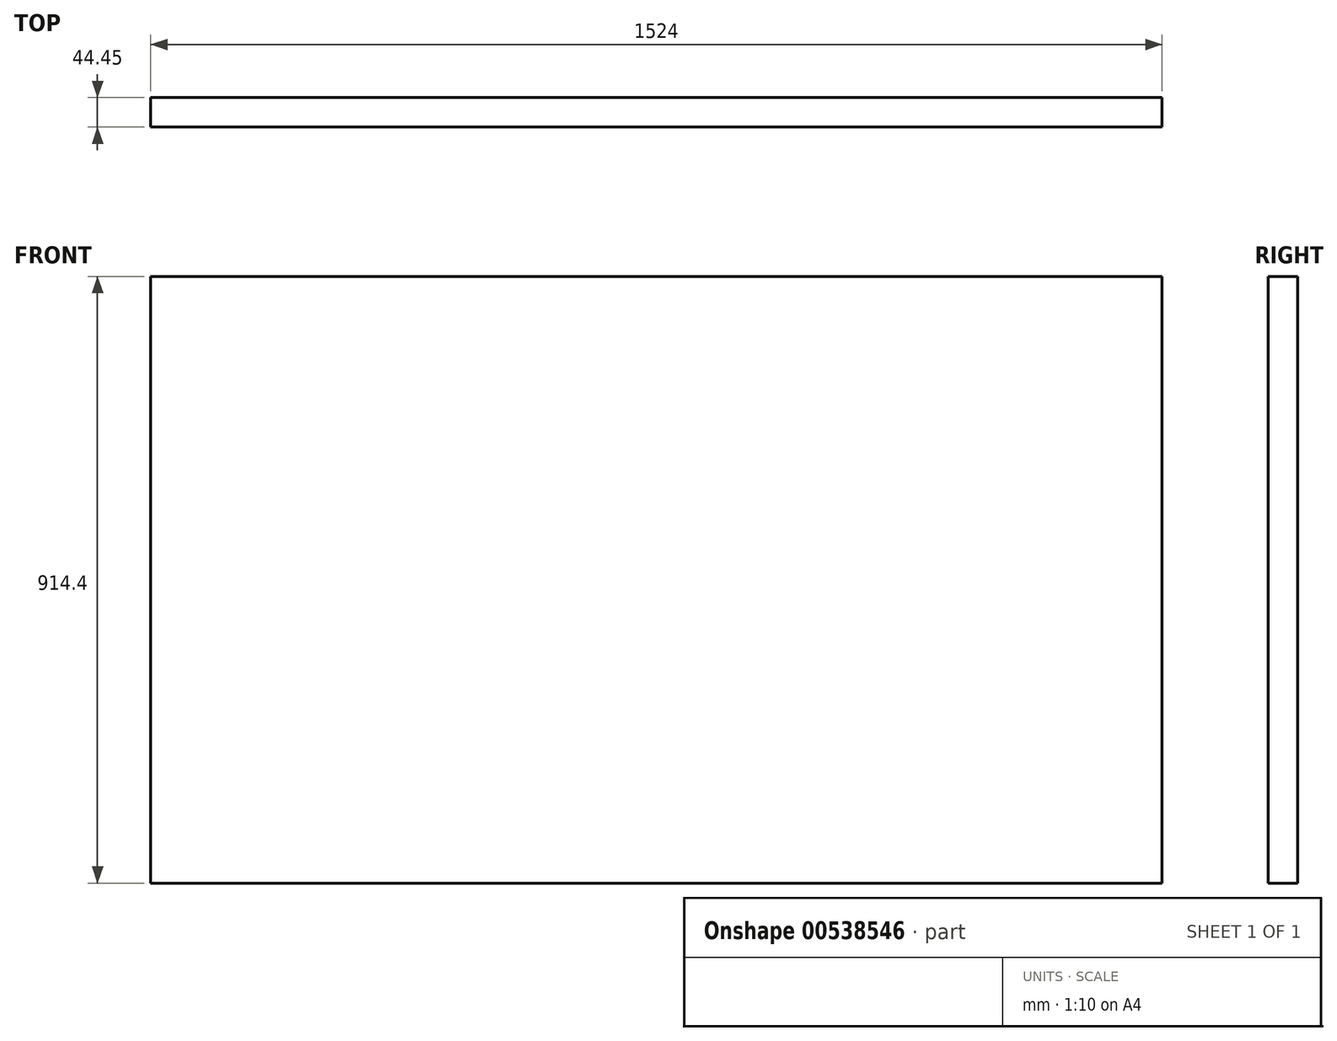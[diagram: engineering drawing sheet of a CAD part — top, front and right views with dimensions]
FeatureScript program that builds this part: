
annotation { "Feature Type Name" : "Feature", "Feature Type Description" : "" }
export const myFeature = defineFeature(function(context is Context, id is Id, definition is map)
    precondition{}
    {
        {
            var Q0;
            Q0=qCreatedBy(makeId("Front.planeOp"),FACE);
            var sketch = newSketch(context, id + "F0", { "sketchPlane" : qUnion([Q0])});
            skLineSegment(sketch, "E0.bottom", {"start": v(-762, 457.2) * mm, "end": v(762, 457.2) * mm});
            skLineSegment(sketch, "E0.top", {"start": v(-762, -457.2) * mm, "end": v(762, -457.2) * mm});
            skLineSegment(sketch, "E0.left", {"start": v(-762, 457.2) * mm, "end": v(-762, -457.2) * mm});
            skLineSegment(sketch, "E0.right", {"start": v(762, 457.2) * mm, "end": v(762, -457.2) * mm});
            skPoint(sketch, "E0.middle", {"position": v(0, 0) * mm});
            skSolve(sketch);
        }
        {
            var Q0;
            Q0 = qSketchRegion(id + "F0", true);
            extrude(context, id + "F1", {"entities" : qUnion([Q0]), "depth" : 44.45 * mm, "offsetDistance" : 25.4 * mm});
        }
    });
